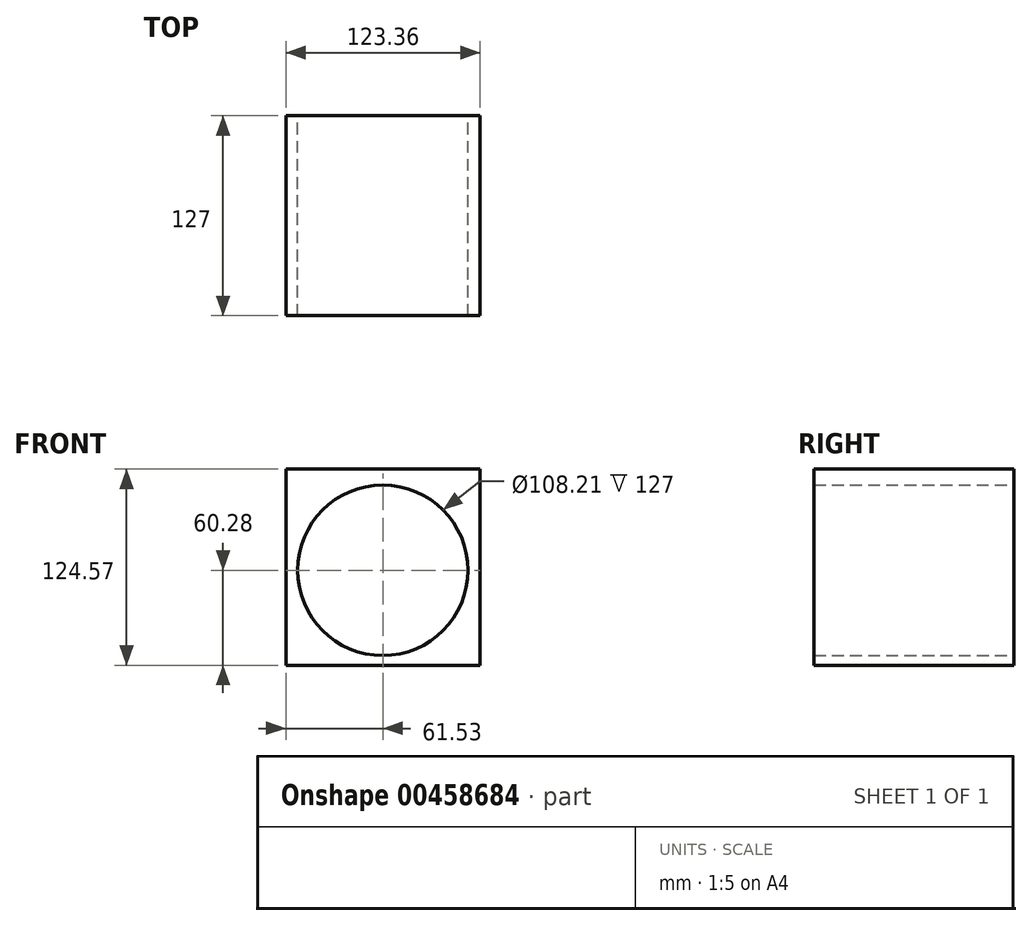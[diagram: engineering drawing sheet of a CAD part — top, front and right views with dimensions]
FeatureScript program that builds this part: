
annotation { "Feature Type Name" : "Feature", "Feature Type Description" : "" }
export const myFeature = defineFeature(function(context is Context, id is Id, definition is map)
    precondition{}
    {
        {
            var Q0;
            Q0=qCreatedBy(makeId("Front.planeOp"),FACE);
            var sketch = newSketch(context, id + "F0", { "sketchPlane" : qUnion([Q0])});
            skCircle(sketch, "E0", {"center": v(0, 0) * mm, "radius": 54.1 * mm});
            skLineSegment(sketch, "E1.bottom", {"start": v(61.83, 64.29) * mm, "end": v(-61.53, 64.29) * mm});
            skLineSegment(sketch, "E1.top", {"start": v(61.83, -60.28) * mm, "end": v(-61.53, -60.28) * mm});
            skLineSegment(sketch, "E1.left", {"start": v(61.83, 64.29) * mm, "end": v(61.83, -60.28) * mm});
            skLineSegment(sketch, "E1.right", {"start": v(-61.53, 64.29) * mm, "end": v(-61.53, -60.28) * mm});
            skSolve(sketch);
        }
        {
            var Q0;
            Q0 = qSketchRegion(id + "F0", true);
            extrude(context, id + "F1", {"entities" : qUnion([Q0]), "depth" : 127 * mm});
        }
        {
            var Q0;
            Q0=qCreatedBy(makeId("Front.planeOp"),FACE);
            var sketch = newSketch(context, id + "F2", { "sketchPlane" : qUnion([Q0])});
            skCircle(sketch, "E2", {"center": v(46.93, 49.28) * mm, "radius": 7.01 * mm});
            skSolve(sketch);
        }
        {
            var Q0;
            Q0=sQuery(id+"F2.wireOp",EDGE,"E2");
            extrude(context, id + "F3", {"bodyType" : ToolBodyType.SURFACE, "surfaceEntities" : qUnion([Q0]), "depth" : 50.8 * mm});
        }
    });
